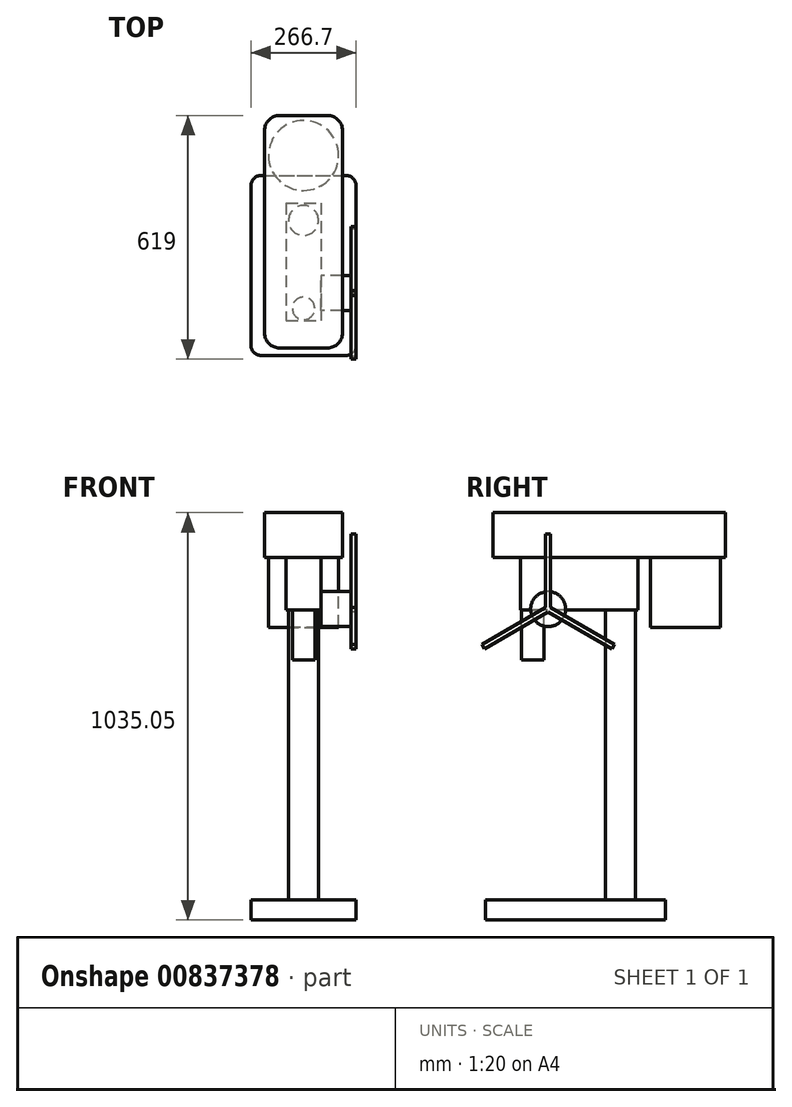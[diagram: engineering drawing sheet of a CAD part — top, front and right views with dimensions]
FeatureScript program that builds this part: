
annotation { "Feature Type Name" : "Feature", "Feature Type Description" : "" }
export const myFeature = defineFeature(function(context is Context, id is Id, definition is map)
    precondition{}
    {
        {
            var Q0;
            Q0=qCreatedBy(makeId("Top.planeOp"),FACE);
            var sketch = newSketch(context, id + "F0", { "sketchPlane" : qUnion([Q0])});
            skLineSegment(sketch, "E0.bottom", {"start": v(-107.95, 114.3) * mm, "end": v(107.95, 114.3) * mm});
            skLineSegment(sketch, "E0.top", {"start": v(-107.95, -342.9) * mm, "end": v(107.95, -342.9) * mm});
            skLineSegment(sketch, "E0.left", {"start": v(-133.35, 88.9) * mm, "end": v(-133.35, -317.5) * mm});
            skLineSegment(sketch, "E0.right", {"start": v(133.35, 88.9) * mm, "end": v(133.35, -317.5) * mm});
            skPoint(sketch, "E1.visualSharp", {"position": v(-133.35, 114.3) * mm});
            skArc(sketch, "E1.filletArc", {"start": v(-107.95, 114.3) * mm, "mid": v(-125.91, 106.86) * mm, "end": v(-133.35, 88.9) * mm});
            skPoint(sketch, "E2.visualSharp", {"position": v(133.35, 114.3) * mm});
            skArc(sketch, "E2.filletArc", {"start": v(133.35, 88.9) * mm, "mid": v(125.91, 106.86) * mm, "end": v(107.95, 114.3) * mm});
            skPoint(sketch, "E3.visualSharp", {"position": v(133.35, -342.9) * mm});
            skArc(sketch, "E3.filletArc", {"start": v(107.95, -342.9) * mm, "mid": v(125.91, -335.46) * mm, "end": v(133.35, -317.5) * mm});
            skPoint(sketch, "E4.visualSharp", {"position": v(-133.35, -342.9) * mm});
            skArc(sketch, "E4.filletArc", {"start": v(-133.35, -317.5) * mm, "mid": v(-125.91, -335.46) * mm, "end": v(-107.95, -342.9) * mm});
            skSolve(sketch);
        }
        {
            var Q0;
            Q0 = qSketchRegion(id + "F0", true);
            extrude(context, id + "F1", {"entities" : qUnion([Q0]), "depth" : 50.8 * mm, "offsetDistance" : 25.4 * mm});
        }
        {
            var Q0;
            Q0=makeQuery(id+"F1.opExtrude","CAP_FACE",FACE,{"disambiguationData":[OSD([sQuery(id+"F0.wireOp",EDGE,"E0.bottom"),sQuery(id+"F0.wireOp",EDGE,"E0.top"),sQuery(id+"F0.wireOp",EDGE,"E0.left"),sQuery(id+"F0.wireOp",EDGE,"E0.right"),sQuery(id+"F0.wireOp",EDGE,"E1.filletArc"),sQuery(id+"F0.wireOp",EDGE,"E2.filletArc"),sQuery(id+"F0.wireOp",EDGE,"E3.filletArc"),sQuery(id+"F0.wireOp",EDGE,"E4.filletArc")])],"isStart":false});
            var sketch = newSketch(context, id + "F2", { "sketchPlane" : qUnion([Q0])});
            skCircle(sketch, "E5", {"center": v(0, 0) * mm, "radius": 38.1 * mm});
            skSolve(sketch);
        }
        {
            var Q0;
            Q0 = qSketchRegion(id + "F2", true);
            extrude(context, id + "F3", {"entities" : qUnion([Q0]), "operationType" : NewBodyOperationType.ADD, "depth" : 736.6 * mm, "offsetDistance" : 25.4 * mm});
        }
        {
            var Q0;
            Q0=makeQuery(id+"F3.opExtrude","CAP_FACE",FACE,{"disambiguationData":[OSD([sQuery(id+"F2.wireOp",EDGE,"E5")])],"isStart":false});
            var sketch = newSketch(context, id + "F4", { "sketchPlane" : qUnion([Q0])});
            skLineSegment(sketch, "E6.bottom", {"start": v(-44.45, 44.45) * mm, "end": v(44.45, 44.45) * mm});
            skLineSegment(sketch, "E6.top", {"start": v(-44.45, -254) * mm, "end": v(44.45, -254) * mm});
            skLineSegment(sketch, "E6.left", {"start": v(-44.45, 44.45) * mm, "end": v(-44.45, -254) * mm});
            skLineSegment(sketch, "E6.right", {"start": v(44.45, 44.45) * mm, "end": v(44.45, -254) * mm});
            skSolve(sketch);
        }
        {
            var Q0;
            Q0 = qSketchRegion(id + "F4", true);
            extrude(context, id + "F5", {"entities" : qUnion([Q0]), "operationType" : NewBodyOperationType.ADD, "depth" : 133.35 * mm, "offsetDistance" : 25.4 * mm});
        }
        {
            var Q0;
            Q0=makeQuery(id+"F5.opExtrude","CAP_FACE",FACE,{"disambiguationData":[OSD([sQuery(id+"F4.wireOp",EDGE,"E6.bottom"),sQuery(id+"F4.wireOp",EDGE,"E6.top"),sQuery(id+"F4.wireOp",EDGE,"E6.left"),sQuery(id+"F4.wireOp",EDGE,"E6.right")])],"isStart":false});
            var sketch = newSketch(context, id + "F6", { "sketchPlane" : qUnion([Q0])});
            skLineSegment(sketch, "E7.bottom", {"start": v(-60.96, 266.7) * mm, "end": v(60.96, 266.7) * mm});
            skLineSegment(sketch, "E7.top", {"start": v(-60.96, -323.85) * mm, "end": v(60.96, -323.85) * mm});
            skLineSegment(sketch, "E7.left", {"start": v(-99.06, 228.6) * mm, "end": v(-99.06, -285.75) * mm});
            skLineSegment(sketch, "E7.right", {"start": v(99.06, 228.6) * mm, "end": v(99.06, -285.75) * mm});
            skPoint(sketch, "E8.visualSharp", {"position": v(-99.06, 266.7) * mm});
            skArc(sketch, "E8.filletArc", {"start": v(-60.96, 266.7) * mm, "mid": v(-87.9, 255.54) * mm, "end": v(-99.06, 228.6) * mm});
            skPoint(sketch, "E9.visualSharp", {"position": v(99.06, 266.7) * mm});
            skArc(sketch, "E9.filletArc", {"start": v(99.06, 228.6) * mm, "mid": v(87.9, 255.54) * mm, "end": v(60.96, 266.7) * mm});
            skPoint(sketch, "E10.visualSharp", {"position": v(99.06, -323.85) * mm});
            skArc(sketch, "E10.filletArc", {"start": v(60.96, -323.85) * mm, "mid": v(87.9, -312.7) * mm, "end": v(99.06, -285.75) * mm});
            skPoint(sketch, "E11.visualSharp", {"position": v(-99.06, -323.85) * mm});
            skArc(sketch, "E11.filletArc", {"start": v(-99.06, -285.75) * mm, "mid": v(-87.9, -312.7) * mm, "end": v(-60.96, -323.85) * mm});
            skSolve(sketch);
        }
        {
            var Q0;
            Q0 = qSketchRegion(id + "F6", true);
            extrude(context, id + "F7", {"entities" : qUnion([Q0]), "operationType" : NewBodyOperationType.ADD, "depth" : 114.3 * mm, "offsetDistance" : 25.4 * mm});
        }
        {
            var Q0;
            Q0=makeQuery(id+"F7.opExtrude","CAP_FACE",FACE,{"disambiguationData":[OSD([sQuery(id+"F6.wireOp",EDGE,"E7.bottom"),sQuery(id+"F6.wireOp",EDGE,"E7.top"),sQuery(id+"F6.wireOp",EDGE,"E7.left"),sQuery(id+"F6.wireOp",EDGE,"E7.right"),sQuery(id+"F6.wireOp",EDGE,"E8.filletArc"),sQuery(id+"F6.wireOp",EDGE,"E9.filletArc"),sQuery(id+"F6.wireOp",EDGE,"E10.filletArc"),sQuery(id+"F6.wireOp",EDGE,"E11.filletArc")])],"isStart":true});
            var sketch = newSketch(context, id + "F8", { "sketchPlane" : qUnion([Q0])});
            skCircle(sketch, "E12", {"center": v(0, -165.1) * mm, "radius": 88.9 * mm});
            skSolve(sketch);
        }
        {
            var Q0;
            Q0 = qSketchRegion(id + "F8", true);
            extrude(context, id + "F9", {"entities" : qUnion([Q0]), "operationType" : NewBodyOperationType.ADD, "depth" : 177.8 * mm, "offsetDistance" : 25.4 * mm});
        }
        {
            var Q0;
            Q0=makeQuery(id+"F5.opExtrude","SWEPT_FACE",FACE,{"disambiguationData":[OSD([sQuery(id+"F4.wireOp",EDGE,"E6.right")])]});
            var sketch = newSketch(context, id + "F10", { "sketchPlane" : qUnion([Q0])});
            skCircle(sketch, "E13", {"center": v(-184.15, 789.94) * mm, "radius": 44.45 * mm});
            skSolve(sketch);
        }
        {
            var Q0;
            Q0 = qSketchRegion(id + "F10", true);
            extrude(context, id + "F11", {"entities" : qUnion([Q0]), "operationType" : NewBodyOperationType.ADD, "depth" : 76.2 * mm, "offsetDistance" : 25.4 * mm});
        }
        {
            var Q0;
            Q0=makeQuery(id+"F11.opExtrude","CAP_FACE",FACE,{"disambiguationData":[OSD([sQuery(id+"F10.wireOp",EDGE,"E13")])],"isStart":false});
            var sketch = newSketch(context, id + "F12", { "sketchPlane" : qUnion([Q0])});
            skLineSegment(sketch, "E14.0", {"start": v(-177.8, 793.6) * mm, "end": v(-177.8, 980.44) * mm});
            skLineSegment(sketch, "E15.0", {"start": v(-190.5, 793.6) * mm, "end": v(-190.5, 980.44) * mm});
            skLineSegment(sketch, "E16.0", {"start": v(-177.8, 793.6) * mm, "end": v(-16, 700.19) * mm});
            skLineSegment(sketch, "E17.0", {"start": v(-184.15, 782.6) * mm, "end": v(-22.35, 689.2) * mm});
            skLineSegment(sketch, "E18.0", {"start": v(-190.5, 793.6) * mm, "end": v(-352.3, 700.19) * mm});
            skLineSegment(sketch, "E19.0", {"start": v(-184.15, 782.6) * mm, "end": v(-345.95, 689.2) * mm});
            skPoint(sketch, "E20.start.orphan", {"position": v(-184.15, 789.94) * mm});
            skLineSegment(sketch, "E21", {"start": v(-22.35, 689.2) * mm, "end": v(-16, 700.19) * mm});
            skLineSegment(sketch, "E22", {"start": v(-190.5, 980.44) * mm, "end": v(-177.8, 980.44) * mm});
            skLineSegment(sketch, "E23", {"start": v(-352.3, 700.19) * mm, "end": v(-345.95, 689.2) * mm});
            skSolve(sketch);
        }
        {
            var Q0;
            Q0 = qSketchRegion(id + "F12", true);
            extrude(context, id + "F13", {"entities" : qUnion([Q0]), "operationType" : NewBodyOperationType.ADD, "depth" : 12.7 * mm, "offsetDistance" : 25.4 * mm});
        }
        {
            var Q0;
            Q0 = qSketchRegion(id + "F12", true);
            extrude(context, id + "F14", {"entities" : qUnion([Q0]), "operationType" : NewBodyOperationType.ADD, "depth" : 12.7 * mm, "offsetDistance" : 25.4 * mm});
        }
        {
            var Q0;
            Q0=makeQuery(id+"F5.opExtrude","CAP_FACE",FACE,{"disambiguationData":[OSD([sQuery(id+"F4.wireOp",EDGE,"E6.bottom"),sQuery(id+"F4.wireOp",EDGE,"E6.top"),sQuery(id+"F4.wireOp",EDGE,"E6.left"),sQuery(id+"F4.wireOp",EDGE,"E6.right")])],"isStart":true});
            var sketch = newSketch(context, id + "F15", { "sketchPlane" : qUnion([Q0])});
            skCircle(sketch, "E24", {"center": v(0, 223.52) * mm, "radius": 28.58 * mm});
            skSolve(sketch);
        }
        {
            var Q0;
            Q0 = qSketchRegion(id + "F15", true);
            extrude(context, id + "F16", {"entities" : qUnion([Q0]), "operationType" : NewBodyOperationType.ADD, "depth" : 127 * mm, "offsetDistance" : 25.4 * mm});
        }
    });
